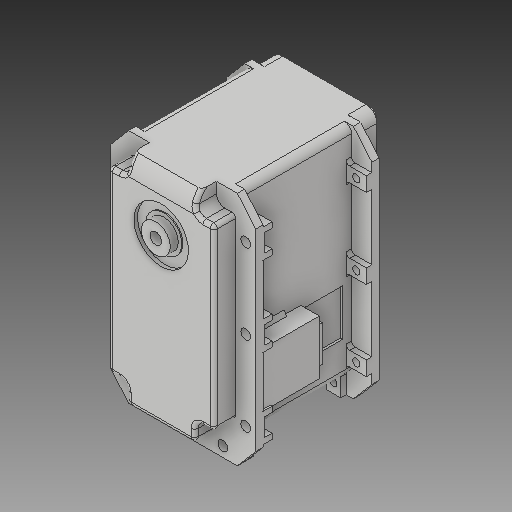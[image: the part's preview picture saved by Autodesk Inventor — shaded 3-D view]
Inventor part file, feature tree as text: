
AUTODESK INVENTOR PART (.ipt)
format: ipt  version: 2019 (Build 230136000, 136)  size: 540,160 bytes
history: native  units: in
note: dims shown in document units (in); Inventor stores cm internally (conversion verified against a paired STEP export)
features: other x3, sketch x1
ambient origin geometry x8: Origin, YZ Plane, XZ Plane, XY Plane, X Axis, Y Axis, Z Axis, Center Point
bodies: Solid1 (feature_tree)
feature tree (4):
  other  "MX-106T.ipt"
  other  "Solid1::MX-106T.ipt"
  other  "TaggingFeature1"
  sketch  "Sketch1"  dims[d0=0.3937in]
